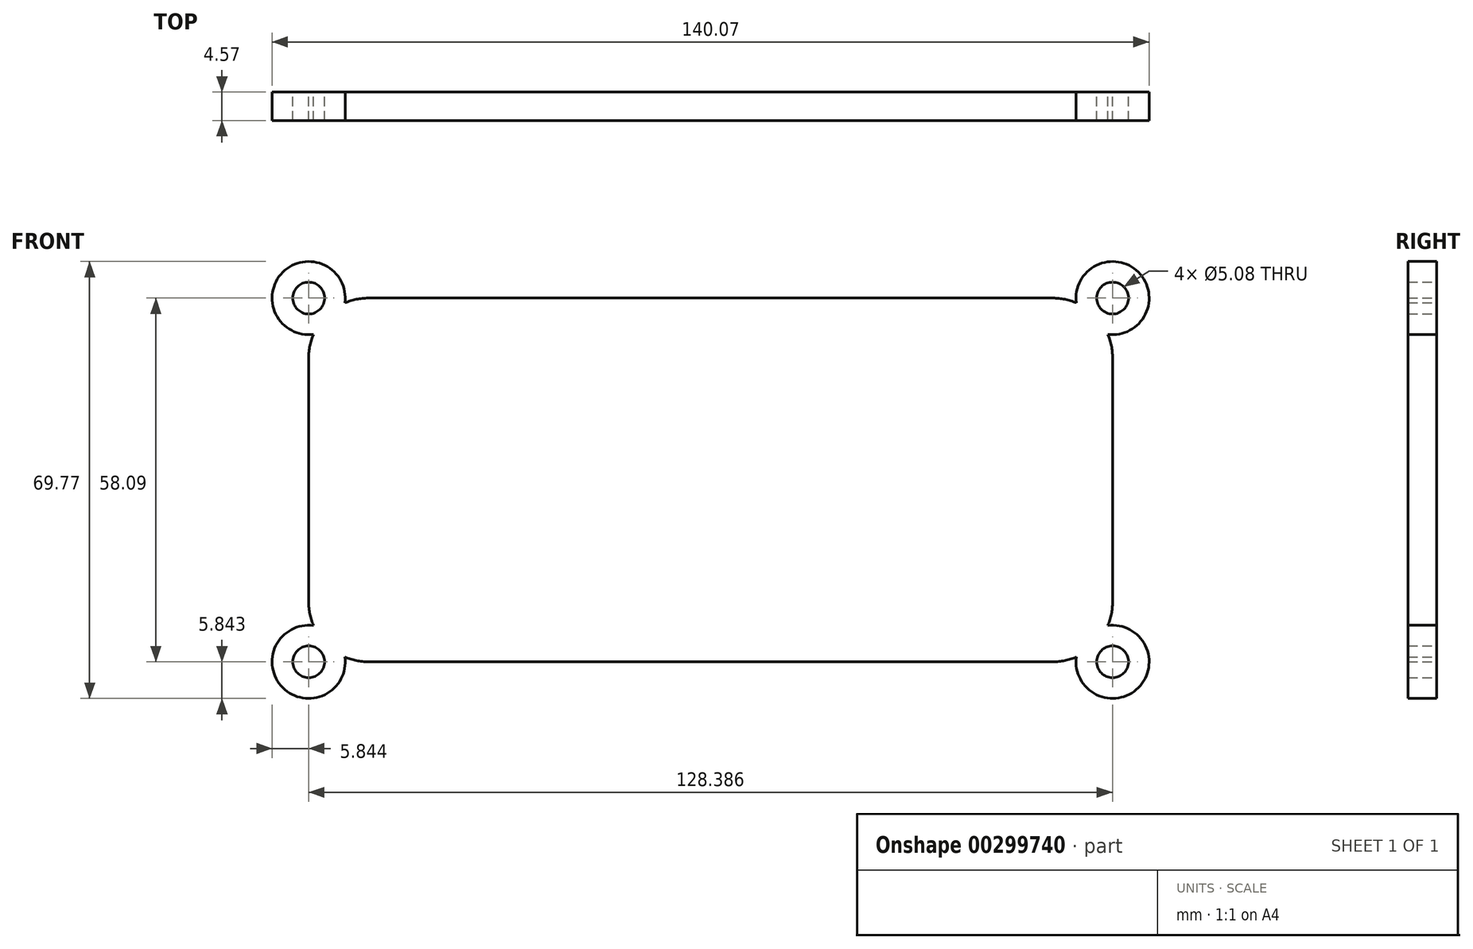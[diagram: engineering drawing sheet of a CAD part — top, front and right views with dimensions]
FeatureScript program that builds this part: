
annotation { "Feature Type Name" : "Feature", "Feature Type Description" : "" }
export const myFeature = defineFeature(function(context is Context, id is Id, definition is map)
    precondition{}
    {
        {
            var Q0;
            Q0=qCreatedBy(makeId("Front.planeOp"),FACE);
            var sketch = newSketch(context, id + "F0", { "sketchPlane" : qUnion([Q0])});
            skCircle(sketch, "E0", {"center": v(0, 0) * mm, "radius": 7.62 * mm, "construction": true});
            skCircle(sketch, "E1", {"center": v(30.48, 0) * mm, "radius": 22.86 * mm, "construction": true});
            skCircle(sketch, "E2", {"center": v(30.48, 0) * mm, "radius": 7.62 * mm, "construction": true});
            skCircle(sketch, "E3", {"center": v(60.96, 0) * mm, "radius": 22.86 * mm, "construction": true});
            skLineSegment(sketch, "E4", {"start": v(0, 45.3) * mm, "end": v(0, -44.68) * mm, "construction": true});
            skLineSegment(sketch, "E5", {"start": v(-57.5, 0) * mm, "end": v(69.76, 0) * mm, "construction": true});
            skCircle(sketch, "E6", {"center": v(60.96, 0) * mm, "radius": 14.26 * mm, "construction": true});
            skCircle(sketch, "E7", {"center": v(0, 0) * mm, "radius": 9.59 * mm, "construction": true});
            skCircle(sketch, "E8", {"center": v(0, 0) * mm, "radius": 25.4 * mm, "construction": true});
            skCircle(sketch, "E9", {"center": v(-36.35, 31.16) * mm, "radius": 2.54 * mm});
            skCircle(sketch, "E10", {"center": v(-36.35, -26.93) * mm, "radius": 2.54 * mm});
            skCircle(sketch, "E11", {"center": v(92.04, 31.16) * mm, "radius": 2.54 * mm});
            skCircle(sketch, "E12", {"center": v(92.04, -26.93) * mm, "radius": 2.54 * mm});
            skLineSegment(sketch, "E13", {"start": v(-36.35, 21.64) * mm, "end": v(-36.35, -17.4) * mm});
            skLineSegment(sketch, "E14", {"start": v(82.52, -26.93) * mm, "end": v(-26.82, -26.93) * mm});
            skLineSegment(sketch, "E15", {"start": v(92.04, 21.64) * mm, "end": v(92.04, -17.4) * mm});
            skLineSegment(sketch, "E16", {"start": v(-26.82, 31.16) * mm, "end": v(82.52, 31.16) * mm});
            skCircle(sketch, "E17.0", {"center": v(-36.35, 31.16) * mm, "radius": 5.84 * mm});
            skCircle(sketch, "E18.0", {"center": v(-36.35, -26.93) * mm, "radius": 5.84 * mm});
            skCircle(sketch, "E19.0", {"center": v(92.04, -26.93) * mm, "radius": 5.84 * mm});
            skCircle(sketch, "E20.0", {"center": v(92.04, 31.16) * mm, "radius": 5.84 * mm});
            skArc(sketch, "E21.filletArc", {"start": v(-26.82, 31.16) * mm, "mid": v(-33.56, 28.37) * mm, "end": v(-36.35, 21.64) * mm});
            skArc(sketch, "E22.filletArc", {"start": v(-36.35, -17.4) * mm, "mid": v(-33.56, -24.14) * mm, "end": v(-26.82, -26.93) * mm});
            skArc(sketch, "E23.filletArc", {"start": v(92.04, 21.64) * mm, "mid": v(89.25, 28.37) * mm, "end": v(82.52, 31.16) * mm});
            skArc(sketch, "E24.filletArc", {"start": v(82.52, -26.93) * mm, "mid": v(89.25, -24.14) * mm, "end": v(92.04, -17.4) * mm});
            skSolve(sketch);
        }
        {
            var Q0;
            Q0 = qSketchRegion(id + "F0", true);
            extrude(context, id + "F1", {"entities" : qUnion([Q0]), "depth" : 4.57 * mm});
        }
    });
